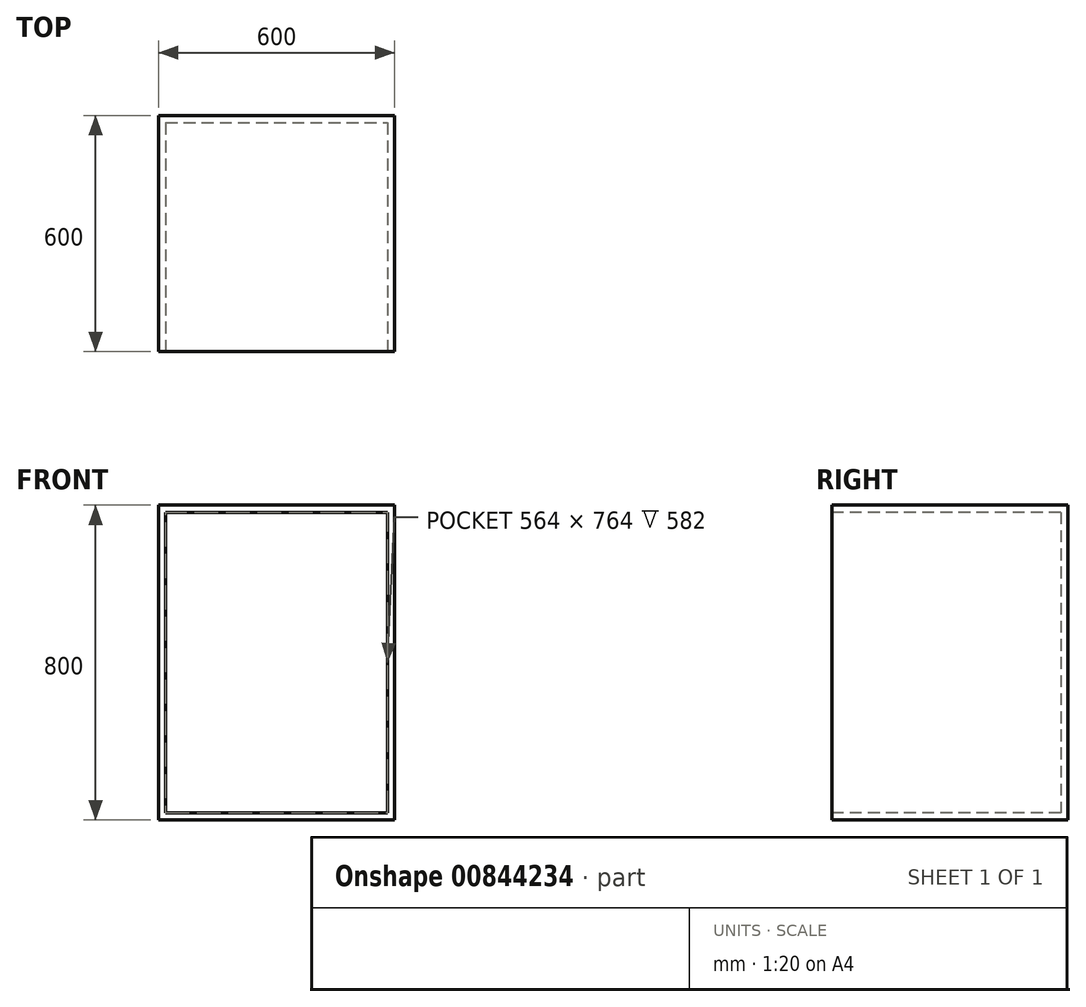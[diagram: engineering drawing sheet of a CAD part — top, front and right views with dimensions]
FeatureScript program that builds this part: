
annotation { "Feature Type Name" : "Feature", "Feature Type Description" : "" }
export const myFeature = defineFeature(function(context is Context, id is Id, definition is map)
    precondition{}
    {
        {
            var Q0;
            Q0=qCreatedBy(makeId("Top.planeOp"),FACE);
            var sketch = newSketch(context, id + "F0", { "sketchPlane" : qUnion([Q0])});
            skLineSegment(sketch, "E0.bottom", {"start": v(0, 0) * mm, "end": v(50.67, 0) * mm});
            skLineSegment(sketch, "E0.top", {"start": v(0, -37.4) * mm, "end": v(50.67, -37.4) * mm});
            skLineSegment(sketch, "E0.left", {"start": v(0, 0) * mm, "end": v(0, -37.4) * mm});
            skLineSegment(sketch, "E0.right", {"start": v(50.67, 0) * mm, "end": v(50.67, -37.4) * mm});
            skSolve(sketch);
        }
        {
            var Q0;
            Q0=makeQuery(id+"F0.imprint","IMPRINT",FACE,{"disambiguationData":[TD([[makeQuery(id+"F0.imprint","IMPRINT",EDGE,{"derivedFrom":sQuery(id+"F0.wireOp",EDGE,"E0.bottom")}),-1.0]])]});
            extrude(context, id + "F1", {"entities" : qUnion([Q0]), "depth" : 800 * mm, "offsetDistance" : 25 * mm});
        }
        {
            var Q0;
            Q0=makeQuery(id+"F1.opExtrude","SWEPT_FACE",FACE,{"disambiguationData":[OSD([sQuery(id+"F0.wireOp",EDGE,"E0.left")])]});
            extrude(context, id + "F2", {"entities" : qUnion([Q0]), "operationType" : NewBodyOperationType.ADD, "oppositeDirection" : true, "depth" : 600 * mm, "offsetDistance" : 25 * mm});
        }
        {
            var Q0;
            {var subQ0=sQuery(id+"F0.wireOp",EDGE,"E0.bottom");Q0=makeQuery(id+"F2.boolean.opBoolean","MERGE",FACE,{"derivedFrom":[makeQuery(id+"F1.opExtrude","SWEPT_FACE",FACE,{"disambiguationData":[OSD([subQ0])]}),makeQuery(id+"F2.opExtrude","SWEPT_FACE",FACE,{"disambiguationData":[OSD([subQ0,sQuery(id+"F0.wireOp",EDGE,"E0.left")])]})]});}
            extrude(context, id + "F3", {"entities" : qUnion([Q0]), "operationType" : NewBodyOperationType.ADD, "oppositeDirection" : true, "depth" : 600 * mm, "offsetDistance" : 25 * mm});
        }
        {
            var Q0;
            Q0=makeQuery(id+"F3.opExtrude","CAP_FACE",FACE,{"disambiguationData":[OSD([sQuery(id+"F0.wireOp",EDGE,"E0.bottom"),sQuery(id+"F0.wireOp",EDGE,"E0.left")])],"isStart":false});
            shell(context, id + "F4", {"entities" : qUnion([Q0]), "thickness" : 18 * mm});
        }
    });
